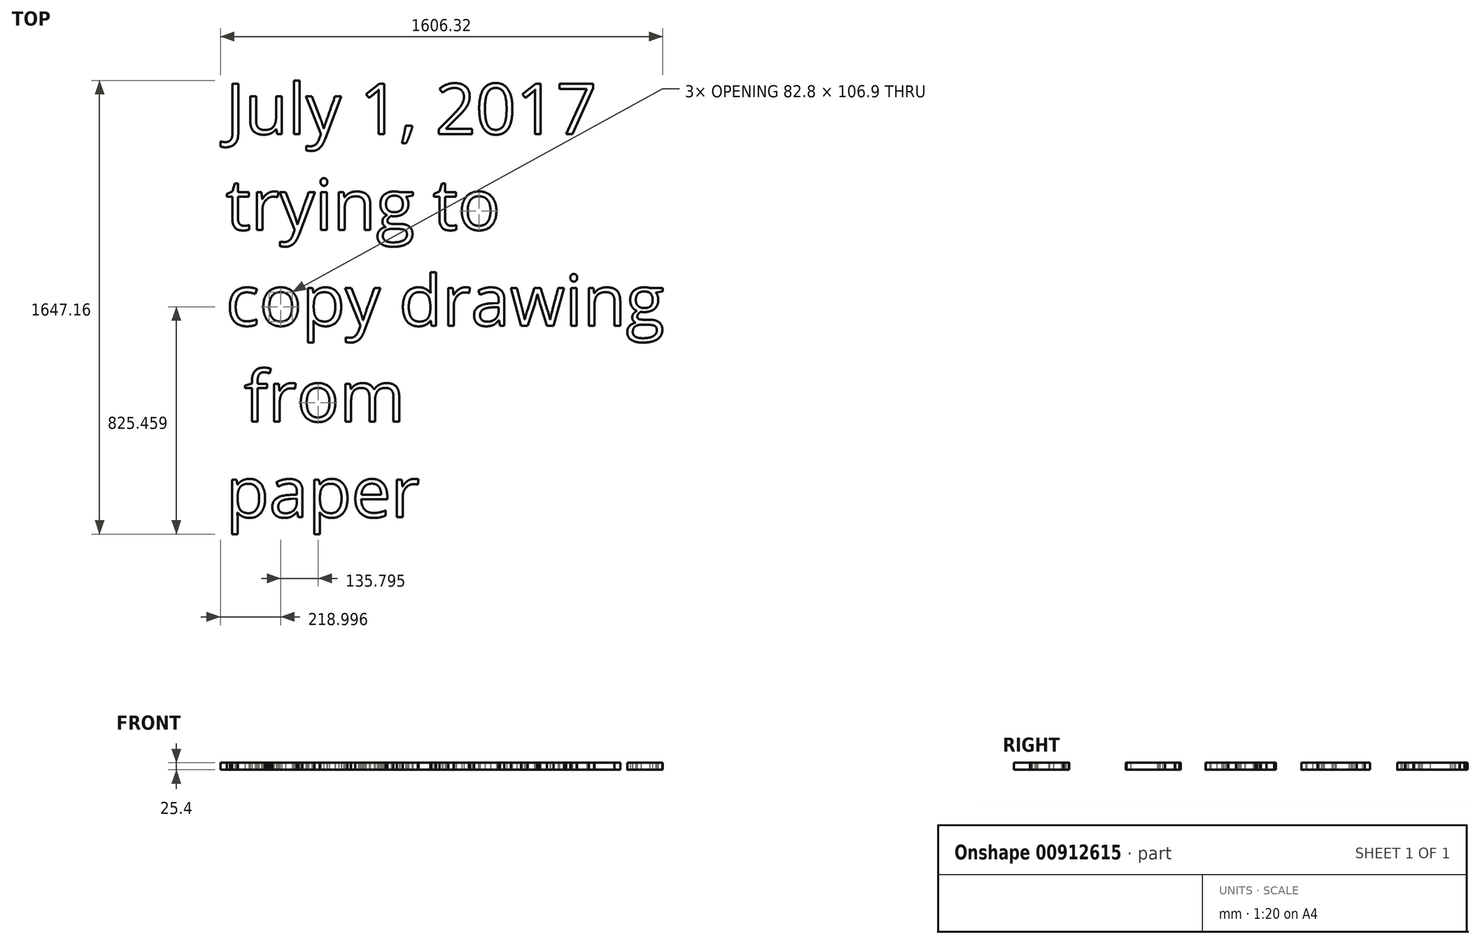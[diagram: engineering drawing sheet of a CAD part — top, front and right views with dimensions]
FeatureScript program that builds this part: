
annotation { "Feature Type Name" : "Feature", "Feature Type Description" : "" }
export const myFeature = defineFeature(function(context is Context, id is Id, definition is map)
    precondition{}
    {
        {
            var Q0;
            Q0=qCreatedBy(makeId("Top.planeOp"),FACE);
            var sketch = newSketch(context, id + "F0", { "sketchPlane" : qUnion([Q0])});
            skText(sketch, "E0", { "text": "July 1, 2017\ntrying to \ncopy drawing\n from \npaper", "fontName": "OpenSans-Regular.ttf"});
            const initialGuessF0  = {"E0": [0.07638, -0.15216, 1, 0, 0.18415]};
            skSetInitialGuess(sketch, initialGuessF0);
            skSolve(sketch);
        }
        {
            var Q0;
            Q0 = qSketchRegion(id + "F0", true);
            extrude(context, id + "F1", {"entities" : qUnion([Q0]), "depth" : 25.4 * mm, "offsetDistance" : 25.4 * mm});
        }
    });
